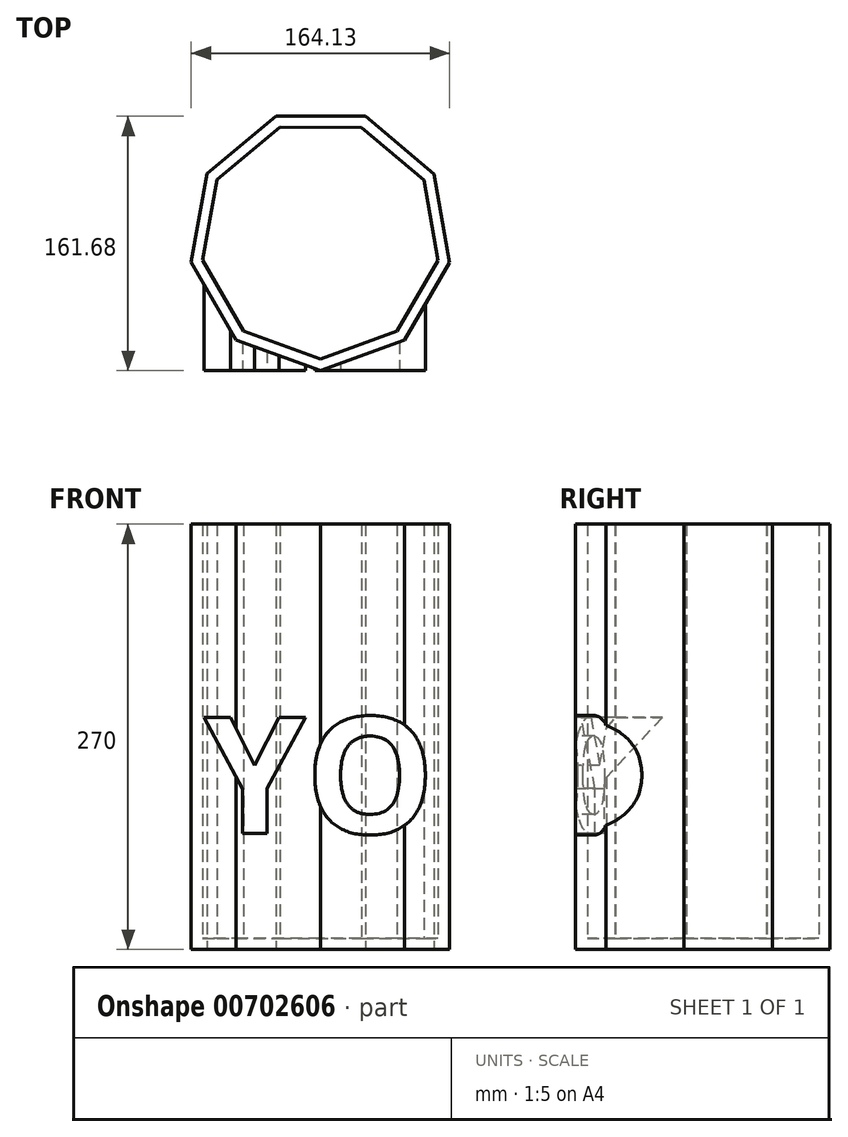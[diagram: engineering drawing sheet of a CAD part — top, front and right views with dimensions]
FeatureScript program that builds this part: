
annotation { "Feature Type Name" : "Feature", "Feature Type Description" : "" }
export const myFeature = defineFeature(function(context is Context, id is Id, definition is map)
    precondition{}
    {
        {
            var Q0;
            Q0=qCreatedBy(makeId("Top.planeOp"),FACE);
            var sketch = newSketch(context, id + "F0", { "sketchPlane" : qUnion([Q0])});
            skCircle(sketch, "E0.cCircle", {"center": v(0, 0) * mm, "radius": 78.3 * mm, "construction": true});
            skLineSegment(sketch, "E0.0", {"start": v(-72.1, 41.78) * mm, "end": v(-28.38, 78.35) * mm});
            skLineSegment(sketch, "E0.1", {"start": v(-28.38, 78.35) * mm, "end": v(28.62, 78.26) * mm});
            skLineSegment(sketch, "E0.2", {"start": v(28.62, 78.26) * mm, "end": v(72.23, 41.55) * mm});
            skLineSegment(sketch, "E0.3", {"start": v(72.23, 41.55) * mm, "end": v(82.04, -14.6) * mm});
            skLineSegment(sketch, "E0.4", {"start": v(82.04, -14.6) * mm, "end": v(53.46, -63.92) * mm});
            skLineSegment(sketch, "E0.5", {"start": v(53.46, -63.92) * mm, "end": v(-0.13, -83.33) * mm});
            skLineSegment(sketch, "E0.6", {"start": v(-0.13, -83.33) * mm, "end": v(-53.66, -63.75) * mm});
            skLineSegment(sketch, "E0.7", {"start": v(-53.66, -63.75) * mm, "end": v(-82.09, -14.34) * mm});
            skLineSegment(sketch, "E0.8", {"start": v(-82.09, -14.34) * mm, "end": v(-72.1, 41.78) * mm});
            skPoint(sketch, "E0.0.midPoint", {"position": v(-50.24, 60.06) * mm});
            skSolve(sketch);
        }
        {
            var Q0;
            Q0 = qSketchRegion(id + "F0", true);
            extrude(context, id + "F1", {"entities" : qUnion([Q0]), "depth" : 270 * mm, "offsetDistance" : 25 * mm});
        }
        {
            var Q0;
            Q0=makeQuery(id+"F1.opExtrude","CAP_FACE",FACE,{"disambiguationData":[OSD([sQuery(id+"F0.wireOp",EDGE,"E0.0"),sQuery(id+"F0.wireOp",EDGE,"E0.1"),sQuery(id+"F0.wireOp",EDGE,"E0.2"),sQuery(id+"F0.wireOp",EDGE,"E0.3"),sQuery(id+"F0.wireOp",EDGE,"E0.4"),sQuery(id+"F0.wireOp",EDGE,"E0.5"),sQuery(id+"F0.wireOp",EDGE,"E0.6"),sQuery(id+"F0.wireOp",EDGE,"E0.7"),sQuery(id+"F0.wireOp",EDGE,"E0.8")])],"isStart":false});
            shell(context, id + "F2", {"entities" : qUnion([Q0]), "thickness" : 7 * mm});
        }
        {
            var Q0;
            Q0=qCreatedBy(makeId("Front.planeOp"),FACE);
            cPlane(context, id + "F3", {"entities" : qUnion([Q0]), "cplaneType" : CPlaneType.OFFSET, "offset" : 83.33 * mm, "width" : 150 * mm, "height" : 150 * mm});
        }
        {
            var Q0;
            Q0=qCreatedBy(id+"F3.planeOp",FACE);
            var sketch = newSketch(context, id + "F4", { "sketchPlane" : qUnion([Q0])});
            skText(sketch, "E1", { "text": "YO", "fontName": "OpenSans-Bold.ttf"});
            const initialGuessF4  = {"E1": [-0.0741, 0.07357, 1, 0, 0.07438]};
            skSetInitialGuess(sketch, initialGuessF4);
            skSolve(sketch);
        }
        {
            var Q0;
            Q0 = qSketchRegion(id + "F4", true);
            var Q1;
            Q1=makeQuery(id+"F1.opExtrude","SWEPT_FACE",FACE,{"disambiguationData":[OSD([sQuery(id+"F0.wireOp",EDGE,"E0.6")])]});
            extrude(context, id + "F5", {"entities" : qUnion([Q0]), "operationType" : NewBodyOperationType.ADD, "endBound" : BoundingType.UP_TO_NEXT, "oppositeDirection" : true, "depth" : 25 * mm, "endBoundEntityFace" : qUnion([Q1]), "offsetDistance" : 25 * mm});
        }
    });
